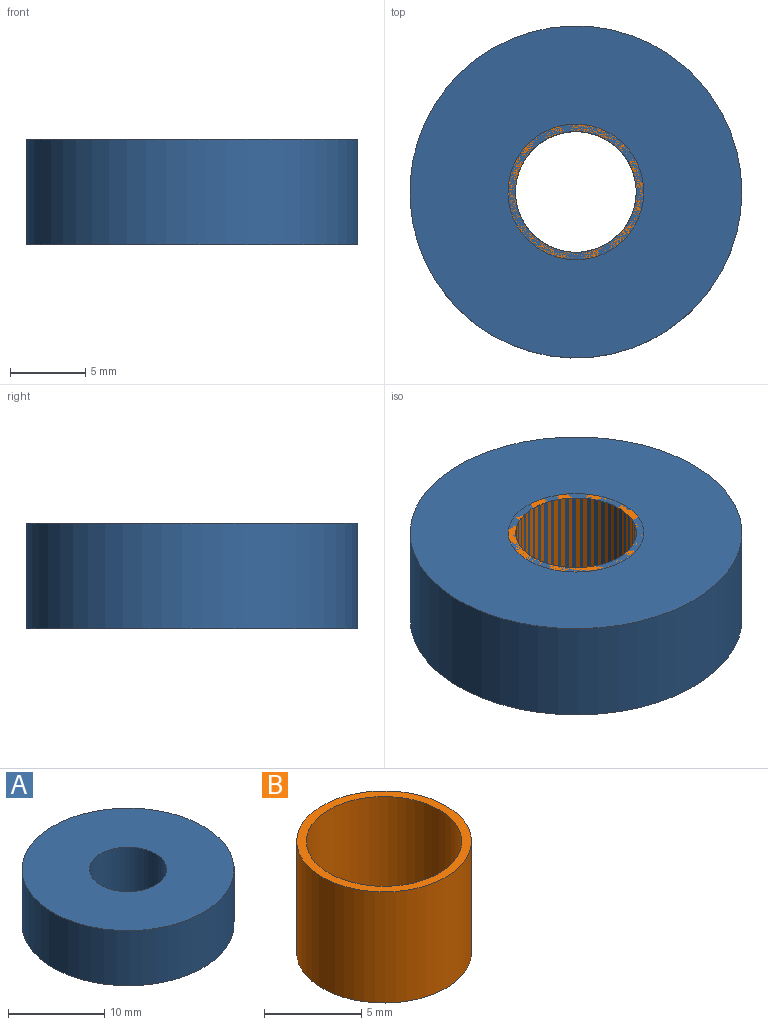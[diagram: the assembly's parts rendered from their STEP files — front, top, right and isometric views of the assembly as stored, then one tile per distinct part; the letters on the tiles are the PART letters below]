
ASSEMBLY  parts=2 mates=1
PART A: 4 faces, bbox 22x22x7 mm
  f0: cylinder r=4mm len=8mm, axis (0,0,-1), area 175.9mm2, adj f2,f3
  f1: cylinder r=11mm len=22mm, axis (0,0,-1), area 483.8mm2, adj f2,f3
  f2: plane 22x22mm, normal (0,0,1), area 329.9mm2, adj f0,f1
  f3: plane 22x22mm, normal (0,0,-1), area 329.9mm2, adj f0,f1
PART B: 4 faces, bbox 9x9x7 mm
  f0: cylinder r=4mm len=8mm, axis (0,0,-1), area 175.9mm2, adj f2,f3
  f1: cylinder r=4.5mm len=9mm, axis (0,0,-1), area 197.9mm2, adj f2,f3
  f2: plane 9x9mm, normal (0,0,1), area 13.4mm2, adj f0,f1
  f3: plane 9x9mm, normal (0,0,-1), area 13.4mm2, adj f0,f1
PLACE A t=(-8.63,-6.01,11.84)mm
PLACE B rot(axis=(0,0,1),90deg) t=(-22.86,49.87,11.84)mm
MATE revolute B.f0 <-> A.f0  axis (0,0,1) through (-47.88,27.9,18.84)mm
